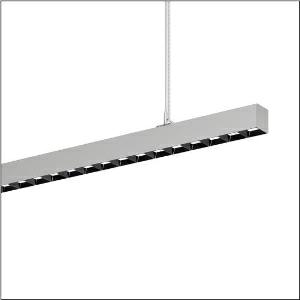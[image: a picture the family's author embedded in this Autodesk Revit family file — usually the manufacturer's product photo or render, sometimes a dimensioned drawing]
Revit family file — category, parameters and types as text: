
# Revit family: silica_21_51mx32dc4dsb
name_source: partatom
category: Lighting Fixtures
units: mm (PartAtom-declared; Revit-internal decimal feet)

## family parameters
Cut with Voids When Loaded = No
Host = Face
Light Source = No
Part Type = Normal
Room Calculation Point = No
Round Connector Dimension = Use Diameter
Shared = No

## types (1)
- --- (1 x LED, 18230 lm, 105.8 W, 4000K)
    Apparent Load = 106 VA
    CIE Flux Codes = 86 99 100 59 100
    Color Rendering = 80
    Color Temperature = 4000K
    Default Elevation = 1800 mm
    Description = Silica 21, office luminaire, primary light control with darklight reflector, of PMMA, black, CAT 2 (L<= 3000cd/m²), light emission: direct/indirect distribution, primary light characteristic: symmetric, installation type: suspended mounting, LED, rated luminous flux: 18.230lm, luminous efficacy: 172lm/W, light colour: 840, colour temperature: 4000K, control gear: DALI 2, with terminal, 3+2-pole, max. 2.5mm², mains connection: 220..240V, AC, 50/60Hz, rated input power: 105.8W, luminaire housing, of aluminium, metallic grey (RAL 9006), length: 3.004mm, width: 53mm, height: 53mm, protection rating (complete): IP20, insulation class (complete): insulation class I (protective earthing), certification: CE, permissible operating ambient temperature: 0..+35°C, standard: EN 50419, packaging unit: 1 piece
    Height = 53 mm
    Lamp = 1 x LED
    Lamp Light Flux = 18230 lm
    Lamp Power = 105.8 W
    Lamp count = 1
    Length = 3004 mm
    Luminous efficacy = 172 lm/W
    Manufacturer = Siteco
    ModVariant = No
    Model = 51MX32DC4DSB
    Mounting Place = Ceiling
    Mounting Type = Pendant
    Number of Poles = 1
    OnlyDefault = Yes
    Power Factor = 1
    Product Name = Silica 21
    Product group = office luminaire | ceiling pendant
    ProductGroupID = 903
    Protection Class = Protection class I
    Protection Degree = IP 20
    RLX_Detail_Level = 1
    RLX_Emergency_Light_Flux = 0 lm
    RLX_Emergency_Type = 0
    RLX_Emergency_Type_DB = No
    RlxData = <blob elided: 65953 chars, md5=631fea42>
    Socket = socket
    Standby Power = 0 W
    System Light Flux = 18230 lm
    System Power = 106 W
    Type Comments = factory setting: luminous flux: 100 % | dim-lin: 254 | 366 mA
    Type Image = l_1335859.jpg
    URL = http://relux.com
    VarID = @adj_123707
    Voltage = 0 V
    Weight = 0.00 kg
    Width = 53 mm

## geometry (parser evidence)
native form markers: Blend x4, Sweep x13
no freeform markers — native parametric forms only
